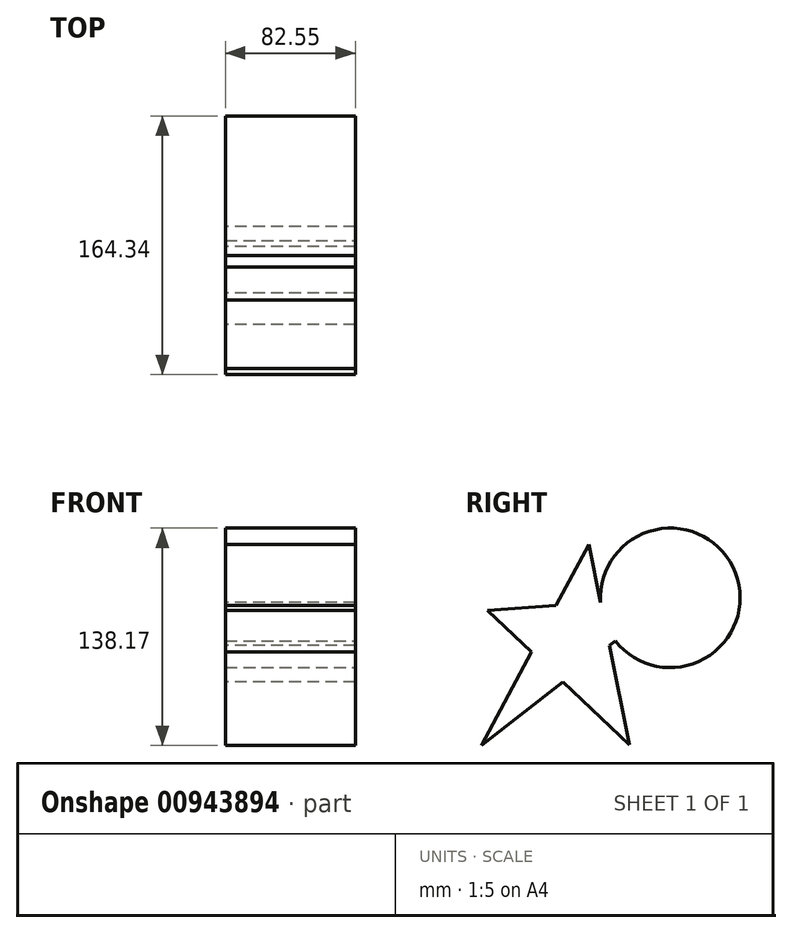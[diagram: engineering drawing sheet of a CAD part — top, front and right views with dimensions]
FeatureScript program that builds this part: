
annotation { "Feature Type Name" : "Feature", "Feature Type Description" : "" }
export const myFeature = defineFeature(function(context is Context, id is Id, definition is map)
    precondition{}
    {
        {
            var Q0;
            Q0=qCreatedBy(makeId("Right.planeOp"),FACE);
            var sketch = newSketch(context, id + "F0", { "sketchPlane" : qUnion([Q0])});
            skLineSegment(sketch, "E0", {"start": v(-83.17, -60.6) * mm, "end": v(-14.89, 67.23) * mm});
            skLineSegment(sketch, "E1", {"start": v(-14.89, 67.23) * mm, "end": v(10.98, -60) * mm});
            skLineSegment(sketch, "E2", {"start": v(10.98, -60) * mm, "end": v(-79.26, 25.42) * mm});
            skLineSegment(sketch, "E3", {"start": v(-79.26, 25.42) * mm, "end": v(36.85, 33.24) * mm});
            skLineSegment(sketch, "E4", {"start": v(36.85, 33.24) * mm, "end": v(-83.17, -60.6) * mm});
            skSolve(sketch);
        }
        {
            var Q0;
            {var subQ1=sQuery(id+"F0.wireOp",EDGE,"E0");var subQ5=sQuery(id+"F0.wireOp",EDGE,"E2");var subQ6=makeQuery(id+"F0.imprint","INTERSECT",VERTEX,{"derivedFrom":[subQ1,subQ5]});Q0=makeQuery(id+"F0.imprint","IMPRINT",FACE,{"disambiguationData":[TD([[makeQuery(id+"F0.imprint","IMPRINT",EDGE,{"disambiguationData":[TD([[subQ6,-1.0]])],"derivedFrom":subQ1}),-1.0]])]});}
            var Q1;
            {var subQ0=sQuery(id+"F0.wireOp",EDGE,"E2");var subQ1=sQuery(id+"F0.wireOp",EDGE,"E1");var subQ2=makeQuery(id+"F0.imprint","INTERSECT",VERTEX,{"derivedFrom":[subQ1,subQ0]});Q1=makeQuery(id+"F0.imprint","IMPRINT",FACE,{"disambiguationData":[TD([[makeQuery(id+"F0.imprint","IMPRINT",EDGE,{"disambiguationData":[TD([[subQ2,1.0]])],"derivedFrom":subQ1}),-1.0]])]});}
            var Q2;
            {var subQ0=sQuery(id+"F0.wireOp",EDGE,"E3");var subQ1=sQuery(id+"F0.wireOp",EDGE,"E1");var subQ2=makeQuery(id+"F0.imprint","INTERSECT",VERTEX,{"derivedFrom":[subQ1,subQ0]});Q2=makeQuery(id+"F0.imprint","IMPRINT",FACE,{"disambiguationData":[TD([[makeQuery(id+"F0.imprint","IMPRINT",EDGE,{"disambiguationData":[TD([[subQ2,-1.0]])],"derivedFrom":subQ1}),1.0]])]});}
            var Q3;
            {var subQ0=sQuery(id+"F0.wireOp",EDGE,"E1");var subQ1=sQuery(id+"F0.wireOp",EDGE,"E0");var subQ2=makeQuery(id+"F0.imprint","INTERSECT",VERTEX,{"derivedFrom":[subQ1,subQ0]});Q3=makeQuery(id+"F0.imprint","IMPRINT",FACE,{"disambiguationData":[TD([[makeQuery(id+"F0.imprint","IMPRINT",EDGE,{"disambiguationData":[TD([[subQ2,1.0]])],"derivedFrom":subQ1}),-1.0]])]});}
            var Q4;
            {var subQ0=sQuery(id+"F0.wireOp",EDGE,"E2");var subQ1=sQuery(id+"F0.wireOp",EDGE,"E0");var subQ2=makeQuery(id+"F0.imprint","INTERSECT",VERTEX,{"derivedFrom":[subQ1,subQ0]});Q4=makeQuery(id+"F0.imprint","IMPRINT",FACE,{"disambiguationData":[TD([[makeQuery(id+"F0.imprint","IMPRINT",EDGE,{"disambiguationData":[TD([[subQ2,-1.0]])],"derivedFrom":subQ1}),1.0]])]});}
            var Q5;
            {var subQ0=sQuery(id+"F0.wireOp",EDGE,"E4");var subQ1=sQuery(id+"F0.wireOp",EDGE,"E0");var subQ2=makeQuery(id+"F0.imprint","INTERSECT",VERTEX,{"derivedFrom":[subQ1,subQ0]});Q5=makeQuery(id+"F0.imprint","IMPRINT",FACE,{"disambiguationData":[TD([[makeQuery(id+"F0.imprint","IMPRINT",EDGE,{"disambiguationData":[TD([[subQ2,-1.0]])],"derivedFrom":subQ1}),-1.0]])]});}
            extrude(context, id + "F1", {"entities" : qUnion([Q0, Q1, Q2, Q3, Q4, Q5]), "depth" : 82.55 * mm, "offsetDistance" : 25.4 * mm});
        }
        {
            var Q0;
            {var subQ0=sQuery(id+"F0.wireOp",EDGE,"E3");Q0=makeQuery(id+"F1.opExtrude","SWEPT_FACE",FACE,{"disambiguationData":[OSD([subQ0]),TDD([makeQuery(id+"F0.imprint","IMPRINT",EDGE,{"disambiguationData":[TD([[makeQuery(id+"F0.imprint","INTERSECT",VERTEX,{"derivedFrom":[subQ0,sQuery(id+"F0.wireOp",EDGE,"E4")]}),1.0]])],"derivedFrom":subQ0})])]});}
            var Q1;
            Q1=makeQuery(id+"F1.opExtrude","SWEPT_EDGE",EDGE,{"disambiguationData":[OSD([sQuery(id+"F0.wireOp",EDGE,"E3"),sQuery(id+"F0.wireOp",EDGE,"E4")])]});
            revolve(context, id + "F2", {"operationType" : NewBodyOperationType.ADD, "surfaceOperationType" : NewSurfaceOperationType.NEW, "entities" : qUnion([Q0]), "axis" : qUnion([Q1]), "revolveType" : RevolveType.FULL});
        }
    });
